# Revit family: Clevertronics_EPIC-1500-SEN-LP
name_source: partatom
category: Lighting Fixtures
units: mm (PartAtom-declared; Revit-internal decimal feet)

## family parameters
Cut with Voids When Loaded = No
Host = Face
Light Source = Yes
Part Type = Normal
Room Calculation Point = No
Round Connector Dimension = Use Diameter
Shared = No

## types (4) — shared parameters
Apparent Load = 0 VA
Clevertronics_AS2293 Classification = C0=D63 C90=D40
Clevertronics_Applicable Standards = AS/NZS3820, CISPR15, AS/NZS60598.1
Clevertronics_Battery = 3.2V 6400mAh
Clevertronics_Battery Type = Lithium Iron Phosphate
Clevertronics_Charger Method = Intelligent current limited constant voltage
Clevertronics_Construction = Powder Coated Sheet Metal Base, Co-extruded IP40 PC Diffuser Assembly, PC End Caps
Clevertronics_Diffuser = Co-extruded IP40 PC Diffuser Assembly
Clevertronics_Dimensions Main Enclosure = L 1533mm x W 72mm x H 78mm
Clevertronics_Driver/ Ballast = LC 57W, 700-1050mA, flexC Ip SNC4
Clevertronics_Earth Leakage = 0.152mA
Clevertronics_Height = 78 mm  [stored 0.255906 ft]
Clevertronics_IP Rating = IP20
Clevertronics_Impact Rating = IK03
Clevertronics_Inrush Current = 28.4A, <88µs
Clevertronics_Length = 1533 mm  [stored 5.02953 ft]
Clevertronics_Material = Clevertronics_Plycarbonate Base
Clevertronics_Mounting = Surface Mount
Clevertronics_Operating Mode = Sustained
Clevertronics_Operating Temperature = 1°C to 40°C
Clevertronics_Operating Voltage = 220-240V~ 50Hz
Clevertronics_Other Modules = Sensor: 1190117
Clevertronics_Power Factor = 0.90 @ High Output
Clevertronics_Replacement Battery = 1550230
Clevertronics_Supply Current = 180mA +/- 20mA
Clevertronics_Total Lumen Output = 6117 lm (128.4 lm/W)
Clevertronics_Weight = 2.2 Kg
Clevertronics_Width = 72 mm  [stored 0.23622 ft]
Color Filter = 16777215
Default Elevation = 1200 mm
Dimming Lamp Color Temperature Shift = <None>
Emit from Line Length = 610 mm
Lamp = Dual LED strip module, 3000K warm white, 5700K cool white, >50,000hr life, Ra>80__L70/B50 Ta 40°C; Reported >54,000hr, Projected 158,000hr__L80/B50 Ta 40°C; Reported >54,000hr, Projected 99,000hr
Manufacturer = Clevertronics
Photometric Web File = EPIC-1500-4K_IESA_G_TUV7191314725_20230817.IES
Tilt Angle = -90.00°
zero-valued in all types: Clevertronics_Annotation Size

## per-type parameters (varying)
| type | Clevertronics_Emergency Driver | Clevertronics_MIC Number | Clevertronics_Power Consumption | Clevertronics_Product Description | Clevertronics_Testing Node | Clevertronics_Testing System | Description | Model |
| EPIC-1500-SEN-LP_AUB02310330001 | LED: 1330069, EM: AUM02370050002 | AUB02310330001 | 0.9/47.6/52.2 (STDYBY/PWR-ON/MAX) | Epic 1500mm Diffused Batten, LP, Motion Sensor, Switchable Colour |  | Clevertest Plus Enabled (Not activated by default) | Epic 1500mm Diffused Batten, LP, Motion Sensor, Switchable Colour | EPIC-1500-SEN-LP |
| EPIC-1500-SEN-LP-HV_AUB02810230001 | LED: 1330069, EM: AUM02870110002 | AUB02810230001 | 47.25W | Epic 1500mm Diffused EmergencyBatten, Motion Sensor, Switchable Colour, Zoneworks XT Hive | 8003191 | Zoneworks XT HIVE (RF) | Epic 1500mm Diffused EmergencyBatten, Motion Sensor, Switchable Colour, Zoneworks XT Hive | EPIC-1500-SEN-LP-HV |
| EPIC-1500-SEN-LP-HVG_AUB02910180001 | LED: 1330069, EM: AUM02970010002 | AUB02910180001 | 47.25W | Epic 1500mm Diffused EmergencyBatten, Motion Sensor, Switchable Colour, Zoneworks XT Hive | 8003580 | Zoneworks XT HIVE (RF) 2.4GHz | Epic 1500mm Diffused EmergencyBatten, Motion Sensor, Switchable Colour, Zoneworks XT Hive | EPIC-1500-SEN-LP-HVG |
| EPIC-1500-SEN-LP-D2_AUB02211210001 | LED: 1330069, EM: AUM02270540001 | AUB02211210001 | 47.25W | Epic 1500mm Diffused EmergencyBatten, Motion Sensor, Switchable Colour, DALI-2 | 8003062 | DALI-2 | Epic 1500mm Diffused EmergencyBatten, Motion Sensor, Switchable Colour, DALI-2 | EPIC-1500-SEN-LP-D2 |

note: [stored X ft] marks values corroborated as IEEE doubles in the binary element streams (Revit-internal decimal feet)

## geometry (parser evidence)
native form markers: Blend x2, Sweep x3
no freeform markers — native parametric forms only
